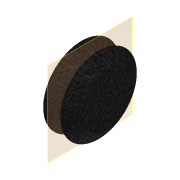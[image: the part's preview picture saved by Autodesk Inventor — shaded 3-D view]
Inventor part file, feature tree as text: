
AUTODESK INVENTOR PART (.ipt)
format: ipt  version: 2019.4 (Build 234330000, 330)  size: 100,864 bytes
history: native  units: mm
features: revolve x1, plane x1, sketch x1
ambient origin geometry x8: Origin, YZ Plane, XZ Plane, XY Plane, X Axis, Y Axis, Z Axis, Center Point
bodies: Solid1 (feature_tree)
feature tree (3):
  revolve  "Revolution1"  [1 undecoded]
  plane  "Work Plane1"
  sketch  "Sketch1"  dims[d0=11.0mm d1=12.4mm d2=8.4mm d3=2.75mm d4=5.5mm d5=2.75mm d6=90.0deg]
note: 1 required parameter value undecoded (feature->parameter linkage not recoverable at this tier; creation-order binding heuristic only, values carry confidence <= 0.55)
